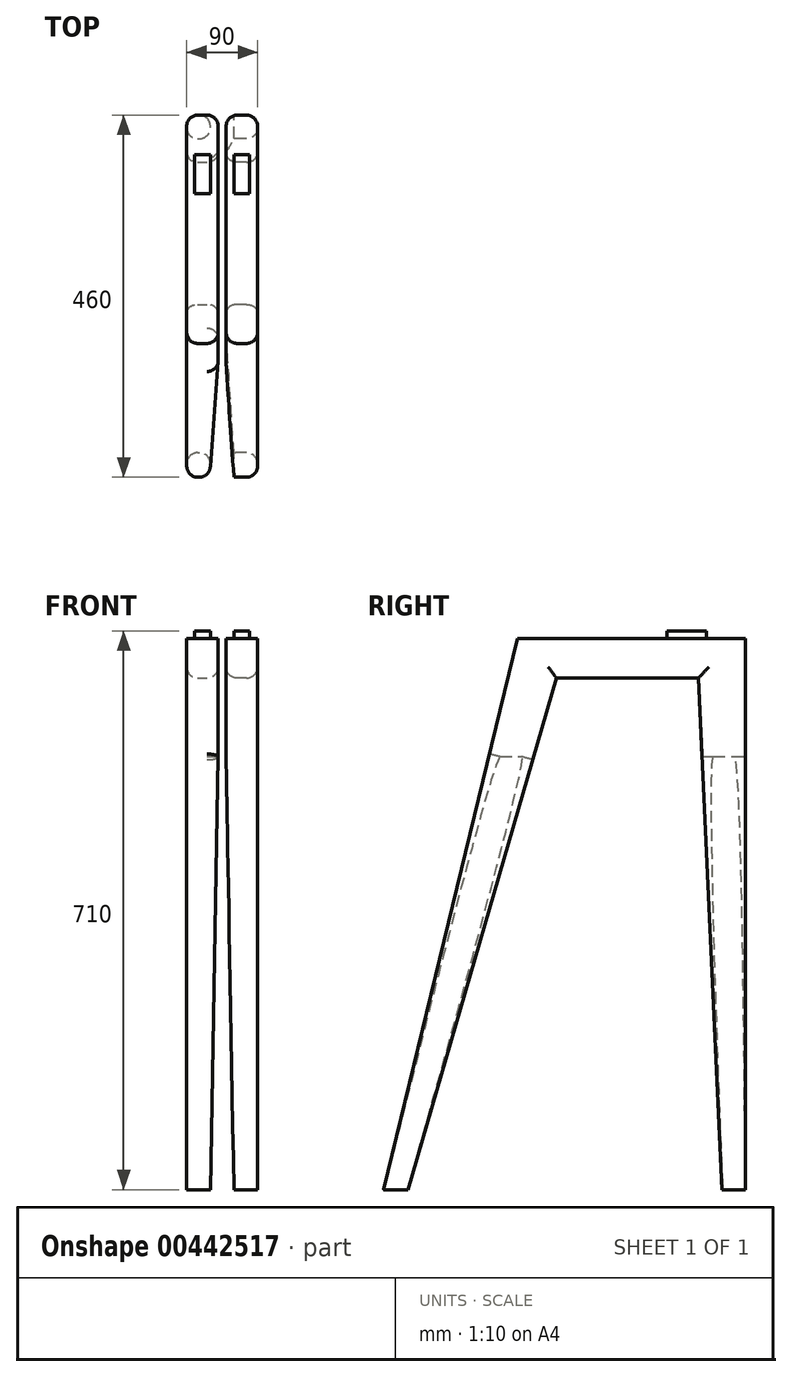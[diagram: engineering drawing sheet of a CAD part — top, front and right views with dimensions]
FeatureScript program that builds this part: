
annotation { "Feature Type Name" : "Feature", "Feature Type Description" : "" }
export const myFeature = defineFeature(function(context is Context, id is Id, definition is map)
    precondition{}
    {
        {
            var Q0;
            Q0=qCreatedBy(makeId("Right.planeOp"),FACE);
            var sketch = newSketch(context, id + "F0", { "sketchPlane" : qUnion([Q0])});
            skLineSegment(sketch, "E0.bottom", {"start": v(0, 0) * mm, "end": v(-600, 0) * mm});
            skLineSegment(sketch, "E0.top", {"start": v(0, 32) * mm, "end": v(-600, 32) * mm});
            skLineSegment(sketch, "E0.left", {"start": v(0, 0) * mm, "end": v(0, 32) * mm});
            skLineSegment(sketch, "E0.right", {"start": v(-600, 0) * mm, "end": v(-600, 32) * mm});
            skSolve(sketch);
        }
        {
            var Q0;
            Q0=qCreatedBy(makeId("Right.planeOp"),FACE);
            var sketch = newSketch(context, id + "F1", { "sketchPlane" : qUnion([Q0])});
            skLineSegment(sketch, "E1", {"start": v(0, 0) * mm, "end": v(-300, 0) * mm, "construction": true});
            skLineSegment(sketch, "E2", {"start": v(0, 0) * mm, "end": v(0, -700) * mm, "construction": true});
            skLineSegment(sketch, "E3", {"start": v(0, 0) * mm, "end": v(-100, 0) * mm, "construction": true});
            skLineSegment(sketch, "E4", {"start": v(-300, 0) * mm, "end": v(-600, 0) * mm, "construction": true});
            skLineSegment(sketch, "E5", {"start": v(-600, 0) * mm, "end": v(-600, -700) * mm, "construction": true});
            skLineSegment(sketch, "E6", {"start": v(-600, -700) * mm, "end": v(-560, -700) * mm, "construction": true});
            skLineSegment(sketch, "E7", {"start": v(-390, 0) * mm, "end": v(-560, -700) * mm});
            skLineSegment(sketch, "E8", {"start": v(-100, 0) * mm, "end": v(-100, -700) * mm});
            skLineSegment(sketch, "E9", {"start": v(0, 0) * mm, "end": v(-133.43, 0) * mm, "construction": true});
            skLineSegment(sketch, "E10", {"start": v(-120, -700) * mm, "end": v(-130, -700) * mm, "construction": true});
            skLineSegment(sketch, "E11", {"start": v(-560, -700) * mm, "end": v(-528.8, -700) * mm});
            skLineSegment(sketch, "E12", {"start": v(-100, -700) * mm, "end": v(-130, -700) * mm});
            skLineSegment(sketch, "E13", {"start": v(-390, 0) * mm, "end": v(-100, 0) * mm});
            skLineSegment(sketch, "E14", {"start": v(-160, -50) * mm, "end": v(-340.4, -50) * mm});
            skPoint(sketch, "E15.orphan", {"position": v(-100, -50) * mm});
            skPoint(sketch, "E16.start.orphan", {"position": v(-150, 0) * mm});
            skPoint(sketch, "E17.start.orphan", {"position": v(-150, -50) * mm});
            skLineSegment(sketch, "E18", {"start": v(-528.8, -700) * mm, "end": v(-340.4, -50) * mm});
            skLineSegment(sketch, "E19", {"start": v(-100, -700) * mm, "end": v(-120, -700) * mm});
            skLineSegment(sketch, "E20", {"start": v(-130, -700) * mm, "end": v(-160, -50) * mm});
            skPoint(sketch, "E21.orphan", {"position": v(-140, -700) * mm});
            skSolve(sketch);
        }
        {
            var Q0;
            Q0 = qSketchRegion(id + "F1", true);
            extrude(context, id + "F2", {"entities" : qUnion([Q0]), "depth" : 40 * mm});
        }
        {
            var Q0;
            Q0=qCreatedBy(makeId("Top.planeOp"),FACE);
            var sketch = newSketch(context, id + "F3", { "sketchPlane" : qUnion([Q0])});
            skLineSegment(sketch, "E22", {"start": v(0, 0) * mm, "end": v(0, -100) * mm, "construction": true});
            skLineSegment(sketch, "E23", {"start": v(0, -100) * mm, "end": v(0, -150) * mm, "construction": true});
            skLineSegment(sketch, "E24", {"start": v(0, -150) * mm, "end": v(10, -150) * mm, "construction": true});
            skLineSegment(sketch, "E25.bottom", {"start": v(10, -150) * mm, "end": v(30, -150) * mm});
            skLineSegment(sketch, "E25.top", {"start": v(10, -200) * mm, "end": v(30, -200) * mm});
            skLineSegment(sketch, "E25.left", {"start": v(10, -150) * mm, "end": v(10, -200) * mm});
            skLineSegment(sketch, "E25.right", {"start": v(30, -150) * mm, "end": v(30, -200) * mm});
            skSolve(sketch);
        }
        {
            var Q0;
            Q0 = qSketchRegion(id + "F3", true);
            extrude(context, id + "F4", {"entities" : qUnion([Q0]), "operationType" : NewBodyOperationType.ADD, "depth" : 10 * mm});
        }
        {
            var Q0;
            Q0=makeQuery(id+"F0.imprint","IMPRINT",FACE,{"disambiguationData":[TD([[makeQuery(id+"F0.imprint","IMPRINT",EDGE,{"derivedFrom":sQuery(id+"F0.wireOp",EDGE,"E0.bottom")}),-1.0]])]});
            cPlane(context, id + "F5", {"entities" : qUnion([Q0]), "cplaneType" : CPlaneType.OFFSET, "offset" : 10 * mm, "oppositeDirection" : true, "width" : 150 * mm, "height" : 150 * mm});
        }
        {
            var Q0;
            Q0=qCreatedBy(id+"F5.planeOp",FACE);
            var sketch = newSketch(context, id + "F6", { "sketchPlane" : qUnion([Q0])});
            skLineSegment(sketch, "E26.0", {"start": v(-560, -700) * mm, "end": v(-390, 0) * mm});
            skLineSegment(sketch, "E26.1", {"start": v(0, 0) * mm, "end": v(-600, 0) * mm});
            skLineSegment(sketch, "E26.2", {"start": v(-100, 0) * mm, "end": v(-100, -700) * mm});
            skLineSegment(sketch, "E26.3", {"start": v(-160, -50) * mm, "end": v(-340.4, -50) * mm});
            skLineSegment(sketch, "E26.4", {"start": v(-130, -700) * mm, "end": v(-160, -50) * mm});
            skLineSegment(sketch, "E26.5", {"start": v(-340.4, -50) * mm, "end": v(-528.8, -700) * mm});
            skLineSegment(sketch, "E26.6", {"start": v(-545.6, -700) * mm, "end": v(-560, -700) * mm});
            skLineSegment(sketch, "E26.7", {"start": v(-528.8, -700) * mm, "end": v(-543.37, -700) * mm});
            skLineSegment(sketch, "E26.8", {"start": v(-545.6, -700) * mm, "end": v(-543.37, -700) * mm});
            skLineSegment(sketch, "E26.9", {"start": v(-115.99, -700) * mm, "end": v(-130, -700) * mm});
            skLineSegment(sketch, "E26.10", {"start": v(-100, -700) * mm, "end": v(-114, -700) * mm});
            skLineSegment(sketch, "E26.11", {"start": v(-114, -700) * mm, "end": v(-115.99, -700) * mm});
            skSolve(sketch);
        }
        {
            var Q0;
            Q0 = qSketchRegion(id + "F6", true);
            extrude(context, id + "F7", {"entities" : qUnion([Q0]), "operationType" : NewBodyOperationType.ADD, "oppositeDirection" : true, "depth" : 40 * mm});
        }
        {
            var Q0;
            Q0=qCreatedBy(makeId("Top.planeOp"),FACE);
            var sketch = newSketch(context, id + "F8", { "sketchPlane" : qUnion([Q0])});
            skLineSegment(sketch, "E27", {"start": v(0, 0) * mm, "end": v(-10, 0) * mm, "construction": true});
            skLineSegment(sketch, "E28", {"start": v(-10, 0) * mm, "end": v(-10, -100) * mm, "construction": true});
            skLineSegment(sketch, "E29", {"start": v(-10, -100) * mm, "end": v(-10, -150) * mm, "construction": true});
            skLineSegment(sketch, "E30", {"start": v(-10, -150) * mm, "end": v(-20, -150) * mm, "construction": true});
            skLineSegment(sketch, "E31.bottom", {"start": v(-20, -150) * mm, "end": v(-40, -150) * mm});
            skLineSegment(sketch, "E31.top", {"start": v(-20, -200) * mm, "end": v(-40, -200) * mm});
            skLineSegment(sketch, "E31.left", {"start": v(-20, -150) * mm, "end": v(-20, -200) * mm});
            skLineSegment(sketch, "E31.right", {"start": v(-40, -150) * mm, "end": v(-40, -200) * mm});
            skSolve(sketch);
        }
        {
            var Q0;
            Q0 = qSketchRegion(id + "F8", true);
            extrude(context, id + "F9", {"entities" : qUnion([Q0]), "operationType" : NewBodyOperationType.ADD, "depth" : 10 * mm});
        }
        {
            var Q0;
            Q0=qCreatedBy(makeId("Front.planeOp"),FACE);
            var sketch = newSketch(context, id + "F10", { "sketchPlane" : qUnion([Q0])});
            skLineSegment(sketch, "E32", {"start": v(0, 0) * mm, "end": v(0, -150) * mm, "construction": true});
            skPoint(sketch, "E33.endSnap0", {"position": v(0, -75) * mm});
            skLineSegment(sketch, "E34", {"start": v(10, -700) * mm, "end": v(0, -700) * mm});
            skLineSegment(sketch, "E35", {"start": v(0, -700) * mm, "end": v(0, -150) * mm});
            skLineSegment(sketch, "E36", {"start": v(0, -150) * mm, "end": v(10, -700) * mm});
            skLineSegment(sketch, "E37", {"start": v(0, -700) * mm, "end": v(-5, -700) * mm, "construction": true});
            skLineSegment(sketch, "E38", {"start": v(-5, -700) * mm, "end": v(-5, -696.38) * mm, "construction": true});
            skLineSegment(sketch, "E39.MirrorCS", {"start": v(20, -699.64) * mm, "end": v(10, -700) * mm, "construction": true});
            skLineSegment(sketch, "E40.MirrorCS", {"start": v(-20, -700) * mm, "end": v(-10, -700) * mm});
            skLineSegment(sketch, "E41.MirrorCS", {"start": v(-10, -150) * mm, "end": v(-20, -700) * mm});
            skLineSegment(sketch, "E42.MirrorCS", {"start": v(-10, -700) * mm, "end": v(-10, -150) * mm});
            skSolve(sketch);
        }
        {
            var Q0;
            Q0 = qSketchRegion(id + "F10", true);
            extrude(context, id + "F11", {"entities" : qUnion([Q0]), "operationType" : NewBodyOperationType.REMOVE, "endBound" : BoundingType.THROUGH_ALL, "depth" : 25 * mm});
        }
        {
            var Q0;
            Q0=qCreatedBy(makeId("Front.planeOp"),FACE);
            var sketch = newSketch(context, id + "F12", { "sketchPlane" : qUnion([Q0])});
            skLineSegment(sketch, "E43", {"start": v(0, 0) * mm, "end": v(0, -150) * mm, "construction": true});
            skLineSegment(sketch, "E44", {"start": v(0, -150) * mm, "end": v(0, -700) * mm, "construction": true});
            skLineSegment(sketch, "E45", {"start": v(0, -700) * mm, "end": v(10, -700) * mm});
            skLineSegment(sketch, "E46", {"start": v(10, -700) * mm, "end": v(0, -150) * mm});
            skLineSegment(sketch, "E47", {"start": v(0, -700) * mm, "end": v(0, -150) * mm});
            skLineSegment(sketch, "E48", {"start": v(10, -700) * mm, "end": v(0, -700) * mm});
            skSolve(sketch);
        }
        {
            var Q0;
            Q0 = qSketchRegion(id + "F12", true);
            extrude(context, id + "F13", {"entities" : qUnion([Q0]), "operationType" : NewBodyOperationType.REMOVE, "endBound" : BoundingType.THROUGH_ALL, "depth" : 25 * mm});
        }
        {
            var Q0;
            Q0=makeQuery(id+"F2.opExtrude","CAP_EDGE",EDGE,{"disambiguationData":[OSD([sQuery(id+"F1.wireOp",EDGE,"E18")])],"isStart":false});
            var Q1;
            Q1=makeQuery(id+"F2.opExtrude","CAP_EDGE",EDGE,{"disambiguationData":[OSD([sQuery(id+"F1.wireOp",EDGE,"E14")])],"isStart":false});
            var Q2;
            Q2=makeQuery(id+"F2.opExtrude","CAP_EDGE",EDGE,{"disambiguationData":[OSD([sQuery(id+"F1.wireOp",EDGE,"E20")])],"isStart":false});
            var Q3;
            Q3=makeQuery(id+"F2.opExtrude","CAP_EDGE",EDGE,{"disambiguationData":[OSD([sQuery(id+"F1.wireOp",EDGE,"E7")])],"isStart":false});
            var Q4;
            Q4=makeQuery(id+"F2.opExtrude","CAP_EDGE",EDGE,{"disambiguationData":[OSD([sQuery(id+"F1.wireOp",EDGE,"E8")])],"isStart":false});
            var Q5;
            Q5=makeQuery(id+"F13.boolean.opBoolean","INTERSECT",EDGE,{"derivedFrom":[makeQuery(id+"F2.opExtrude","SWEPT_FACE",FACE,{"disambiguationData":[OSD([sQuery(id+"F1.wireOp",EDGE,"E8")])]}),makeQuery(id+"F13.opExtrude","SWEPT_FACE",FACE,{"disambiguationData":[OSD([sQuery(id+"F12.wireOp",EDGE,"E46")])]})]});
            var Q6;
            Q6=makeQuery(id+"F2.opExtrude","CAP_EDGE",EDGE,{"disambiguationData":[OSD([sQuery(id+"F1.wireOp",EDGE,"E8")])],"isStart":true});
            var Q7;
            Q7=makeQuery(id+"F2.opExtrude","CAP_EDGE",EDGE,{"disambiguationData":[OSD([sQuery(id+"F1.wireOp",EDGE,"E18")])],"isStart":true});
            var Q8;
            Q8=makeQuery(id+"F13.boolean.opBoolean","INTERSECT",EDGE,{"derivedFrom":[makeQuery(id+"F2.opExtrude","SWEPT_FACE",FACE,{"disambiguationData":[OSD([sQuery(id+"F1.wireOp",EDGE,"E18")])]}),makeQuery(id+"F13.opExtrude","SWEPT_FACE",FACE,{"disambiguationData":[OSD([sQuery(id+"F12.wireOp",EDGE,"E46")])]})]});
            var Q9;
            Q9=makeQuery(id+"F11.boolean.opBoolean","INTERSECT",EDGE,{"derivedFrom":[makeQuery(id+"F7.opExtrude","SWEPT_FACE",FACE,{"disambiguationData":[OSD([sQuery(id+"F6.wireOp",EDGE,"E26.5")])]}),makeQuery(id+"F11.opExtrude","SWEPT_FACE",FACE,{"disambiguationData":[OSD([sQuery(id+"F10.wireOp",EDGE,"E41.MirrorCS")])]})]});
            var Q10;
            Q10=makeQuery(id+"F7.opExtrude","CAP_EDGE",EDGE,{"disambiguationData":[OSD([sQuery(id+"F6.wireOp",EDGE,"E26.5")])],"isStart":true});
            var Q11;
            Q11=makeQuery(id+"F7.opExtrude","CAP_EDGE",EDGE,{"disambiguationData":[OSD([sQuery(id+"F6.wireOp",EDGE,"E26.3")])],"isStart":true});
            var Q12;
            Q12=makeQuery(id+"F7.opExtrude","CAP_EDGE",EDGE,{"disambiguationData":[OSD([sQuery(id+"F6.wireOp",EDGE,"E26.2")])],"isStart":true});
            var Q13;
            Q13=makeQuery(id+"F11.boolean.opBoolean","INTERSECT",EDGE,{"derivedFrom":[makeQuery(id+"F7.opExtrude","SWEPT_FACE",FACE,{"disambiguationData":[OSD([sQuery(id+"F6.wireOp",EDGE,"E26.2")])]}),makeQuery(id+"F11.opExtrude","SWEPT_FACE",FACE,{"disambiguationData":[OSD([sQuery(id+"F10.wireOp",EDGE,"E41.MirrorCS")])]})]});
            var Q14;
            Q14=makeQuery(id+"F7.opExtrude","CAP_EDGE",EDGE,{"disambiguationData":[OSD([sQuery(id+"F6.wireOp",EDGE,"E26.2")])],"isStart":false});
            var Q15;
            Q15=makeQuery(id+"F2.opExtrude","CAP_EDGE",EDGE,{"disambiguationData":[OSD([sQuery(id+"F1.wireOp",EDGE,"E14")])],"isStart":true});
            var Q16;
            Q16=makeQuery(id+"F7.opExtrude","CAP_EDGE",EDGE,{"disambiguationData":[OSD([sQuery(id+"F6.wireOp",EDGE,"E26.4")])],"isStart":false});
            var Q17;
            Q17=makeQuery(id+"F7.opExtrude","CAP_EDGE",EDGE,{"disambiguationData":[OSD([sQuery(id+"F6.wireOp",EDGE,"E26.3")])],"isStart":false});
            var Q18;
            Q18=makeQuery(id+"F7.opExtrude","CAP_EDGE",EDGE,{"disambiguationData":[OSD([sQuery(id+"F6.wireOp",EDGE,"E26.5")])],"isStart":false});
            var Q19;
            Q19=makeQuery(id+"F7.opExtrude","CAP_EDGE",EDGE,{"disambiguationData":[OSD([sQuery(id+"F6.wireOp",EDGE,"E26.4")])],"isStart":true});
            var Q20;
            Q20=makeQuery(id+"F2.opExtrude","CAP_EDGE",EDGE,{"disambiguationData":[OSD([sQuery(id+"F1.wireOp",EDGE,"E20")])],"isStart":true});
            var Q21;
            Q21=makeQuery(id+"F13.boolean.opBoolean","INTERSECT",EDGE,{"derivedFrom":[makeQuery(id+"F2.opExtrude","SWEPT_FACE",FACE,{"disambiguationData":[OSD([sQuery(id+"F1.wireOp",EDGE,"E20")])]}),makeQuery(id+"F13.opExtrude","SWEPT_FACE",FACE,{"disambiguationData":[OSD([sQuery(id+"F12.wireOp",EDGE,"E46")])]})]});
            var Q22;
            Q22=makeQuery(id+"F11.boolean.opBoolean","INTERSECT",EDGE,{"derivedFrom":[makeQuery(id+"F7.opExtrude","SWEPT_FACE",FACE,{"disambiguationData":[OSD([sQuery(id+"F6.wireOp",EDGE,"E26.4")])]}),makeQuery(id+"F11.opExtrude","SWEPT_FACE",FACE,{"disambiguationData":[OSD([sQuery(id+"F10.wireOp",EDGE,"E41.MirrorCS")])]})]});
            var Q23;
            Q23=makeQuery(id+"F7.opExtrude","CAP_EDGE",EDGE,{"disambiguationData":[OSD([sQuery(id+"F6.wireOp",EDGE,"E26.0")])],"isStart":true});
            var Q24;
            Q24=makeQuery(id+"F2.opExtrude","CAP_EDGE",EDGE,{"disambiguationData":[OSD([sQuery(id+"F1.wireOp",EDGE,"E7")])],"isStart":true});
            var Q25;
            Q25=makeQuery(id+"F13.boolean.opBoolean","INTERSECT",EDGE,{"derivedFrom":[makeQuery(id+"F2.opExtrude","SWEPT_FACE",FACE,{"disambiguationData":[OSD([sQuery(id+"F1.wireOp",EDGE,"E7")])]}),makeQuery(id+"F13.opExtrude","SWEPT_FACE",FACE,{"disambiguationData":[OSD([sQuery(id+"F12.wireOp",EDGE,"E46")])]})]});
            var Q26;
            Q26=makeQuery(id+"F11.boolean.opBoolean","INTERSECT",EDGE,{"derivedFrom":[makeQuery(id+"F7.opExtrude","SWEPT_FACE",FACE,{"disambiguationData":[OSD([sQuery(id+"F6.wireOp",EDGE,"E26.0")])]}),makeQuery(id+"F11.opExtrude","SWEPT_FACE",FACE,{"disambiguationData":[OSD([sQuery(id+"F10.wireOp",EDGE,"E41.MirrorCS")])]})]});
            var Q27;
            Q27=makeQuery(id+"F7.opExtrude","CAP_EDGE",EDGE,{"disambiguationData":[OSD([sQuery(id+"F6.wireOp",EDGE,"E26.0")])],"isStart":false});
            fillet(context, id + "F14", {"entities" : qUnion([Q0, Q1, Q2, Q3, Q4, Q5, Q6, Q7, Q8, Q9, Q10, Q11, Q12, Q13, Q14, Q15, Q16, Q17, Q18, Q19, Q20, Q21, Q22, Q23, Q24, Q25, Q26, Q27]), "radius" : 14 * mm, "tangentPropagation" : true, "allowEdgeOverflow" : false});
        }
    });
